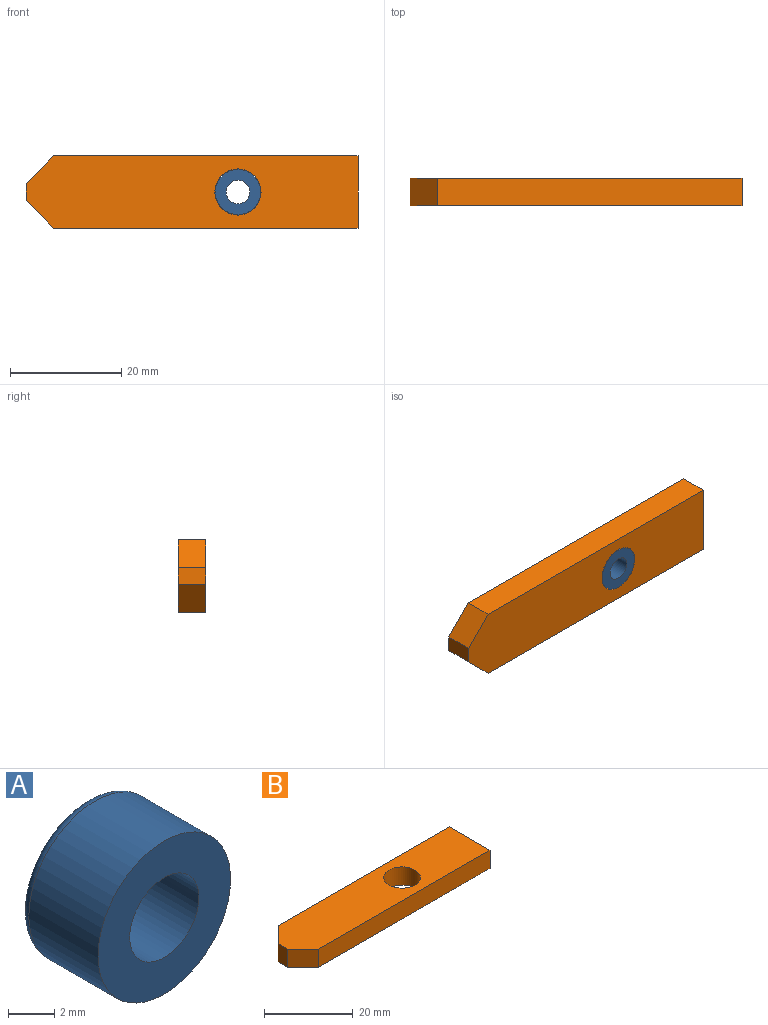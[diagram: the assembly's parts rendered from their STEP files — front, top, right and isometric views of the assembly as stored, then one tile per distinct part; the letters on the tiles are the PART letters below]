
ASSEMBLY  parts=2 mates=1
PART A: 5 faces, bbox 8.8x4.8x8.8 mm
  f0: cylinder r=4.06mm len=8.13mm, axis (0,-1,0), area 108.3mm2, adj f1,f2
  f1: torus R=3.56mm, axis (0,1,0), area 19.5mm2, adj f0,f3
  f2: plane 8.13x8.13mm, normal (0,-1,0), area 37.8mm2, adj f0,f4
  f3: plane 7.11x7.11mm, normal (0,1,0), area 25.6mm2, adj f1,f4
  f4: cylinder r=2.12mm len=4.75mm, axis (0,-1,0), area 63.3mm2, adj f2,f3
PART B: 9 faces, bbox 59.7x13x5 mm
  f0: plane 54.67x5mm, normal (0,1,0), area 273.4mm2, adj f2,f3,f7,f8
  f1: plane 54.67x5mm, normal (0,-1,0), area 273.4mm2, adj f2,f3,f6,f8
  f2: plane 59.67x13mm, normal (0,0,1), area 696.6mm2, adj f0,f1,f4,f5,f6,f7,f8
  f3: plane 59.67x13mm, normal (0,0,-1), area 696.6mm2, adj f0,f1,f4,f5,f6,f7,f8
  f4: plane 5x3mm, normal (-1,0,0), area 15mm2, adj f2,f3,f6,f7
  f5: cylinder r=4.15mm len=8.3mm, axis (0,0,-1), area 130.4mm2, adj f2,f3
  f6: plane 5x5mm, normal (-0.71,-0.71,0), area 35.4mm2, adj f1,f2,f3,f4
  f7: plane 5x5mm, normal (-0.71,0.71,0), area 35.4mm2, adj f0,f2,f3,f4
  f8: plane 13x5mm, normal (1,0,0), area 65mm2, adj f0,f1,f2,f3
PLACE A rot(axis=(1,0,0),0deg) t=(0.77,4.58,0.23)mm
PLACE B rot(axis=(1,0,0),90deg) t=(0.77,7.21,0.23)mm
MATE fastened A.f0 <-> B.f5  axis (0,-1,0) through (0.77,2.21,0.23)mm
